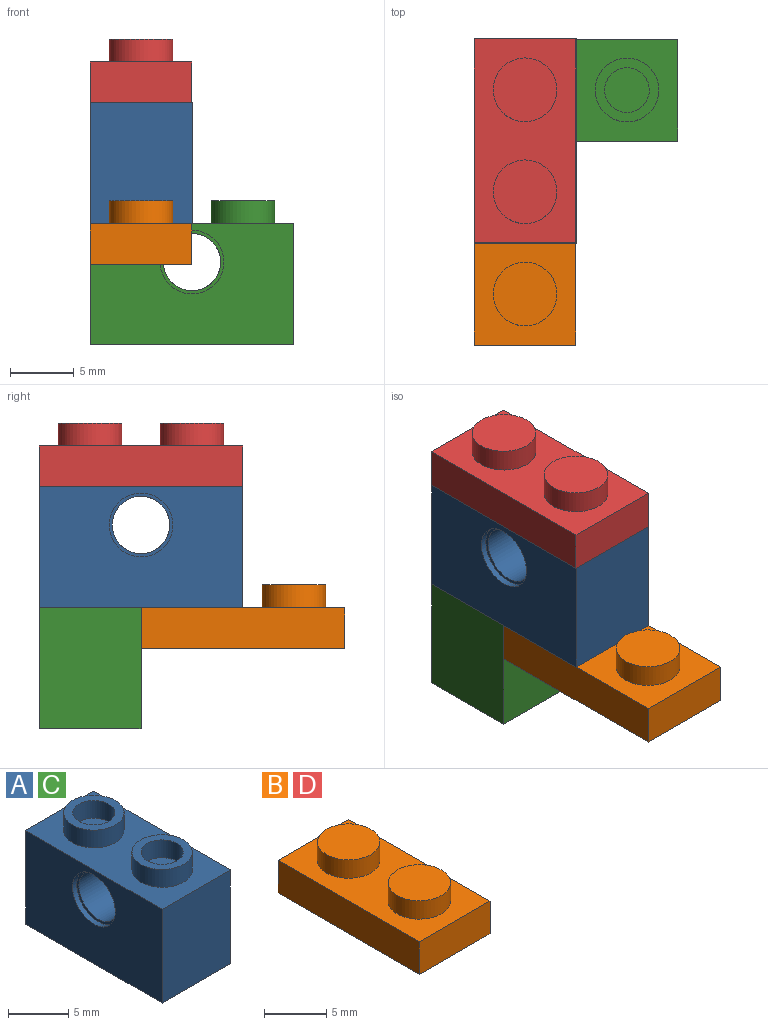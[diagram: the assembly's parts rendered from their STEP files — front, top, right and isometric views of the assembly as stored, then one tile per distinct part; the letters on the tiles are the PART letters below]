
ASSEMBLY  parts=4 mates=3
PART A: 30 faces, bbox 8x16x11.3 mm
  f0: cylinder r=3mm len=6mm, axis (1,0,0), area 55.5mm2, adj f3,f7,f9,f12,f27
  f1: plane 16x9.5mm, normal (-1,0,0), area 132.4mm2, adj f4,f5,f11,f13,f24
  f2: cylinder r=2.25mm len=7mm, axis (1,0,0), area 99mm2, adj f23,f25
  f3: plane 5x3.9mm, normal (0,0,-1), area 19.5mm2, adj f0,f6,f7,f9
  f4: plane 9.5x8mm, normal (0,1,0), area 76mm2, adj f1,f10,f11,f13
  f5: plane 9.5x8mm, normal (0,-1,0), area 76mm2, adj f1,f10,f11,f13
  f6: plane 8x5mm, normal (0,1,0), area 40mm2, adj f3,f7,f9,f11
  f7: plane 13x8mm, normal (1,0,0), area 81.3mm2, adj f0,f3,f6,f8,f11,f12
  f8: plane 8x5mm, normal (0,-1,0), area 40mm2, adj f7,f9,f11,f12
  f9: plane 13x8mm, normal (-1,0,0), area 81.3mm2, adj f0,f3,f6,f8,f11,f12
  f10: plane 16x9.5mm, normal (1,0,0), area 132.4mm2, adj f4,f5,f11,f13,f22
  f11: plane 16x8mm, normal (0,0,-1), area 63mm2, adj f1,f4,f5,f6,f7,f8,f9,f10
  f12: plane 5x3.9mm, normal (0,0,-1), area 19.5mm2, adj f0,f7,f8,f9
  f13: plane 16x8mm, normal (0,0,1), area 88.7mm2, adj f1,f4,f5,f10,f15,f19
  f14: cylinder r=1.75mm len=3.5mm, axis (0,0,-1), area 19.8mm2, adj f16,f17
  f15: cylinder r=2.5mm len=5mm, axis (0,0,-1), area 28.3mm2, adj f13,f16
  f16: plane 5x5mm, normal (0,0,1), area 10mm2, adj f14,f15
  f17: plane 3.5x3.5mm, normal (0,0,1), area 9.6mm2, adj f14
  f18: cylinder r=1.75mm len=3.5mm, axis (0,0,-1), area 19.8mm2, adj f20,f21
  f19: cylinder r=2.5mm len=5mm, axis (0,0,-1), area 28.3mm2, adj f13,f20
  f20: plane 5x5mm, normal (0,0,1), area 10mm2, adj f18,f19
  f21: plane 3.5x3.5mm, normal (0,0,1), area 9.6mm2, adj f18
  f22: cylinder r=2.5mm len=5mm, axis (1,0,0), area 7.9mm2, adj f10,f23
  f23: plane 5x5mm, normal (1,0,0), area 3.7mm2, adj f2,f22
  f24: cylinder r=2.5mm len=5mm, axis (-1,0,0), area 7.9mm2, adj f1,f25
  f25: plane 5x5mm, normal (-1,0,0), area 3.7mm2, adj f2,f24
  f26: cylinder r=0.75mm len=3.6mm, axis (0,0,-1), area 16.7mm2, adj f28,f29
  f27: cylinder r=1.5mm len=3.9mm, axis (0,0,-1), area 34.8mm2, adj f0,f28
  f28: plane 3x3mm, normal (0,0,-1), area 5.3mm2, adj f26,f27
  f29: cylinder r=3mm len=1.5mm, axis (1,0,0), area 1.8mm2, adj f26
PART B: 23 faces, bbox 8x16x5 mm
  f0: plane 16x3.2mm, normal (-1,0,0), area 51.2mm2, adj f1,f7,f8,f10
  f1: plane 8x3.2mm, normal (0,-1,0), area 25.6mm2, adj f0,f2,f8,f10
  f2: plane 16x3.2mm, normal (1,0,0), area 51.2mm2, adj f1,f7,f8,f10
  f3: plane 4.4x2mm, normal (0,1,0), area 8.8mm2, adj f4,f6,f8,f9
  f4: plane 12.4x2mm, normal (1,0,0), area 24.8mm2, adj f3,f5,f8,f9
  f5: plane 4.4x2mm, normal (0,-1,0), area 8.8mm2, adj f4,f6,f8,f9
  f6: plane 12.4x2mm, normal (-1,0,0), area 24.8mm2, adj f3,f5,f8,f9
  f7: plane 8x3.2mm, normal (0,1,0), area 25.6mm2, adj f0,f2,f8,f10
  f8: plane 16x8mm, normal (0,0,-1), area 73.4mm2, adj f0,f1,f2,f3,f4,f5,f6,f7
  f9: plane 12.4x4.4mm, normal (0,0,-1), area 37.7mm2, adj f3,f4,f5,f6,f15,f19,f21
  f10: plane 16x8mm, normal (0,0,1), area 88.7mm2, adj f0,f1,f2,f7,f11,f13
  f11: cylinder r=2.5mm len=5mm, axis (0,0,-1), area 28.3mm2, adj f10,f12
  f12: plane 5x5mm, normal (0,0,1), area 19.6mm2, adj f11
  f13: cylinder r=2.5mm len=5mm, axis (0,0,-1), area 28.3mm2, adj f10,f14
  f14: plane 5x5mm, normal (0,0,1), area 19.6mm2, adj f13
  f15: cylinder r=1.5mm len=3mm, axis (0,0,1), area 18.8mm2, adj f9,f17
  f16: cylinder r=0.75mm len=2mm, axis (0,0,1), area 9.4mm2, adj f17,f18
  f17: plane 3x3mm, normal (0,0,-1), area 5.3mm2, adj f15,f16
  f18: plane 1.5x1.5mm, normal (0,0,-1), area 1.8mm2, adj f16
  f19: cylinder r=1.25mm len=2.5mm, axis (0,0,-1), area 11.8mm2, adj f9,f20
  f20: plane 2.5x2.5mm, normal (0,0,-1), area 4.9mm2, adj f19
  f21: cylinder r=1.25mm len=2.5mm, axis (0,0,-1), area 11.8mm2, adj f9,f22
  f22: plane 2.5x2.5mm, normal (0,0,-1), area 4.9mm2, adj f21
PART C: same geometry as A
PART D: same geometry as B
PLACE A t=(24.95,-25.85,11.93)mm
PLACE B t=(-8.73,-19.39,8.73)mm
PLACE C rot(axis=(0,0,1),90deg) t=(-2.03,10.99,2.43)mm
PLACE D t=(-8.73,-11.39,21.43)mm
MATE fastened B.f11 <-> D.f13  axis (0,0,1) through (-6.96,-28.92,13.73)mm
MATE fastened C.f18 <-> D.f11  axis (0,0,1) through (-6.96,-20.92,11.93)mm
MATE fastened A.f18 <-> D.f11  axis (0,0,1) through (-6.96,-20.92,21.43)mm
